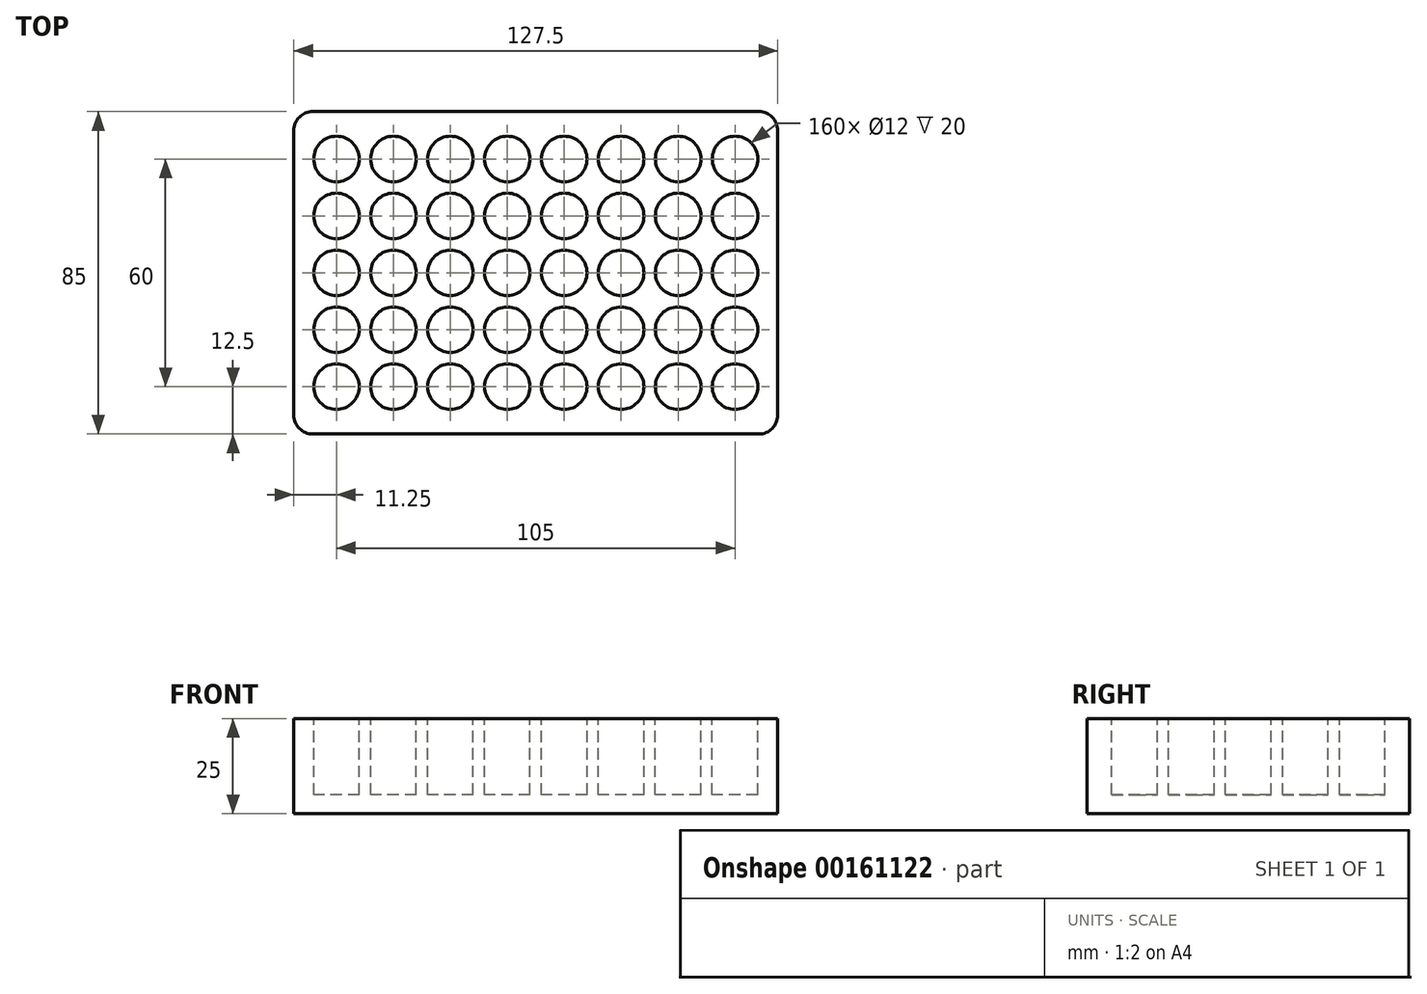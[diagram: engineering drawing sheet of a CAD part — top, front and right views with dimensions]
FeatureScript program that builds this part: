
annotation { "Feature Type Name" : "Feature", "Feature Type Description" : "" }
export const myFeature = defineFeature(function(context is Context, id is Id, definition is map)
    precondition{}
    {
        {
            var Q0;
            Q0=qCreatedBy(makeId("Top.planeOp"),FACE);
            var sketch = newSketch(context, id + "F0", { "sketchPlane" : qUnion([Q0])});
            skLineSegment(sketch, "E0.bottom", {"start": v(58.75, -42.5) * mm, "end": v(-58.75, -42.5) * mm});
            skLineSegment(sketch, "E0.top", {"start": v(58.75, 42.5) * mm, "end": v(-58.75, 42.5) * mm});
            skLineSegment(sketch, "E0.left", {"start": v(63.75, -37.5) * mm, "end": v(63.75, 37.5) * mm});
            skLineSegment(sketch, "E0.right", {"start": v(-63.75, -37.5) * mm, "end": v(-63.75, 37.5) * mm});
            skPoint(sketch, "E0.middle", {"position": v(0, 0) * mm});
            skPoint(sketch, "E1.visualSharp", {"position": v(-63.75, 42.5) * mm});
            skArc(sketch, "E1.filletArc", {"start": v(-58.75, 42.5) * mm, "mid": v(-62.29, 41.04) * mm, "end": v(-63.75, 37.5) * mm});
            skPoint(sketch, "E2.visualSharp", {"position": v(-63.75, -42.5) * mm});
            skArc(sketch, "E2.filletArc", {"start": v(-63.75, -37.5) * mm, "mid": v(-62.29, -41.04) * mm, "end": v(-58.75, -42.5) * mm});
            skPoint(sketch, "E3.visualSharp", {"position": v(63.75, -42.5) * mm});
            skArc(sketch, "E3.filletArc", {"start": v(58.75, -42.5) * mm, "mid": v(62.29, -41.04) * mm, "end": v(63.75, -37.5) * mm});
            skPoint(sketch, "E4.visualSharp", {"position": v(63.75, 42.5) * mm});
            skArc(sketch, "E4.filletArc", {"start": v(63.75, 37.5) * mm, "mid": v(62.29, 41.04) * mm, "end": v(58.75, 42.5) * mm});
            skSolve(sketch);
        }
        {
            var Q0;
            Q0 = qSketchRegion(id + "F0", true);
            extrude(context, id + "F1", {"entities" : qUnion([Q0]), "depth" : 25 * mm});
        }
        {
            var Q0;
            Q0=makeQuery(id+"F1.opExtrude","CAP_FACE",FACE,{"disambiguationData":[OSD([sQuery(id+"F0.wireOp",EDGE,"E0.bottom"),sQuery(id+"F0.wireOp",EDGE,"E0.top"),sQuery(id+"F0.wireOp",EDGE,"E0.left"),sQuery(id+"F0.wireOp",EDGE,"E0.right"),sQuery(id+"F0.wireOp",EDGE,"E1.filletArc"),sQuery(id+"F0.wireOp",EDGE,"E2.filletArc"),sQuery(id+"F0.wireOp",EDGE,"E3.filletArc"),sQuery(id+"F0.wireOp",EDGE,"E4.filletArc")])],"isStart":false});
            var sketch = newSketch(context, id + "F2", { "sketchPlane" : qUnion([Q0])});
            skCircle(sketch, "E5", {"center": v(-52.5, 30) * mm, "radius": 6 * mm});
            skCircle(sketch, "E6.0.1.0", {"center": v(-52.5, 15) * mm, "radius": 6 * mm});
            skCircle(sketch, "E6.0.2.0", {"center": v(-52.5, 0) * mm, "radius": 6 * mm});
            skCircle(sketch, "E6.0.3.0", {"center": v(-52.5, -15) * mm, "radius": 6 * mm});
            skCircle(sketch, "E6.0.4.0", {"center": v(-52.5, -30) * mm, "radius": 6 * mm});
            skCircle(sketch, "E6.1.0.0", {"center": v(-37.5, 30) * mm, "radius": 6 * mm});
            skCircle(sketch, "E6.1.1.0", {"center": v(-37.5, 15) * mm, "radius": 6 * mm});
            skCircle(sketch, "E6.1.2.0", {"center": v(-37.5, 0) * mm, "radius": 6 * mm});
            skCircle(sketch, "E6.1.3.0", {"center": v(-37.5, -15) * mm, "radius": 6 * mm});
            skCircle(sketch, "E6.1.4.0", {"center": v(-37.5, -30) * mm, "radius": 6 * mm});
            skCircle(sketch, "E6.2.0.0", {"center": v(-22.5, 30) * mm, "radius": 6 * mm});
            skCircle(sketch, "E6.2.1.0", {"center": v(-22.5, 15) * mm, "radius": 6 * mm});
            skCircle(sketch, "E6.2.2.0", {"center": v(-22.5, 0) * mm, "radius": 6 * mm});
            skCircle(sketch, "E6.2.3.0", {"center": v(-22.5, -15) * mm, "radius": 6 * mm});
            skCircle(sketch, "E6.2.4.0", {"center": v(-22.5, -30) * mm, "radius": 6 * mm});
            skCircle(sketch, "E6.3.0.0", {"center": v(-7.5, 30) * mm, "radius": 6 * mm});
            skCircle(sketch, "E6.3.1.0", {"center": v(-7.5, 15) * mm, "radius": 6 * mm});
            skCircle(sketch, "E6.3.2.0", {"center": v(-7.5, 0) * mm, "radius": 6 * mm});
            skCircle(sketch, "E6.3.3.0", {"center": v(-7.5, -15) * mm, "radius": 6 * mm});
            skCircle(sketch, "E6.3.4.0", {"center": v(-7.5, -30) * mm, "radius": 6 * mm});
            skCircle(sketch, "E6.4.0.0", {"center": v(7.5, 30) * mm, "radius": 6 * mm});
            skCircle(sketch, "E6.4.1.0", {"center": v(7.5, 15) * mm, "radius": 6 * mm});
            skCircle(sketch, "E6.4.2.0", {"center": v(7.5, 0) * mm, "radius": 6 * mm});
            skCircle(sketch, "E6.4.3.0", {"center": v(7.5, -15) * mm, "radius": 6 * mm});
            skCircle(sketch, "E6.4.4.0", {"center": v(7.5, -30) * mm, "radius": 6 * mm});
            skCircle(sketch, "E6.5.0.0", {"center": v(22.5, 30) * mm, "radius": 6 * mm});
            skCircle(sketch, "E6.5.1.0", {"center": v(22.5, 15) * mm, "radius": 6 * mm});
            skCircle(sketch, "E6.5.2.0", {"center": v(22.5, 0) * mm, "radius": 6 * mm});
            skCircle(sketch, "E6.5.3.0", {"center": v(22.5, -15) * mm, "radius": 6 * mm});
            skCircle(sketch, "E6.5.4.0", {"center": v(22.5, -30) * mm, "radius": 6 * mm});
            skCircle(sketch, "E6.6.0.0", {"center": v(37.5, 30) * mm, "radius": 6 * mm});
            skCircle(sketch, "E6.6.1.0", {"center": v(37.5, 15) * mm, "radius": 6 * mm});
            skCircle(sketch, "E6.6.2.0", {"center": v(37.5, 0) * mm, "radius": 6 * mm});
            skCircle(sketch, "E6.6.3.0", {"center": v(37.5, -15) * mm, "radius": 6 * mm});
            skCircle(sketch, "E6.6.4.0", {"center": v(37.5, -30) * mm, "radius": 6 * mm});
            skCircle(sketch, "E6.7.0.0", {"center": v(52.5, 30) * mm, "radius": 6 * mm});
            skCircle(sketch, "E6.7.1.0", {"center": v(52.5, 15) * mm, "radius": 6 * mm});
            skCircle(sketch, "E6.7.2.0", {"center": v(52.5, 0) * mm, "radius": 6 * mm});
            skCircle(sketch, "E6.7.3.0", {"center": v(52.5, -15) * mm, "radius": 6 * mm});
            skCircle(sketch, "E6.7.4.0", {"center": v(52.5, -30) * mm, "radius": 6 * mm});
            skLineSegment(sketch, "E6.direction1", {"start": v(-52.5, 30) * mm, "end": v(-37.5, 30) * mm, "construction": true});
            skLineSegment(sketch, "E6.direction2", {"start": v(-52.5, 30) * mm, "end": v(-52.5, 15) * mm, "construction": true});
            skSolve(sketch);
        }
        {
            var Q0;
            Q0 = qSketchRegion(id + "F2", true);
            extrude(context, id + "F3", {"entities" : qUnion([Q0]), "operationType" : NewBodyOperationType.REMOVE, "oppositeDirection" : true, "depth" : 20 * mm});
        }
    });
